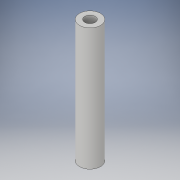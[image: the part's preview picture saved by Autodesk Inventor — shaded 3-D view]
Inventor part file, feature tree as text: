
AUTODESK INVENTOR PART (.ipt)
format: ipt  version: 2019 (Build 230136000, 136)  size: 95,232 bytes
history: native  units: mm
features: other x1, extrude x1, sketch x1
ambient origin geometry x8: Origin, YZ Plane, XZ Plane, XY Plane, X Axis, Y Axis, Z Axis, Center Point
bodies: Body1 (feature_tree)
feature tree (3):
  other  "Bryła1"
  extrude  "Wyciągnięcie proste1"  Depth=3.0mm
  sketch  "Szkic1"
